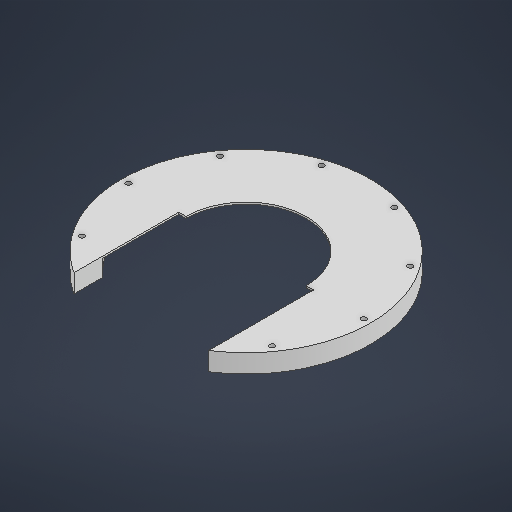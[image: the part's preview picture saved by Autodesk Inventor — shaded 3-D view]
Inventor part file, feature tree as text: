
AUTODESK INVENTOR PART (.ipt)
format: ipt  version: 2025 (Build 290162000, 162)  size: 236,544 bytes
history: native  units: in
note: dims shown in document units (in); Inventor stores cm internally (conversion verified against a paired STEP export)
features: sketch x5, extrude x3, hole x1
ambient origin geometry x8: Origin, YZ Plane, XZ Plane, XY Plane, X Axis, Y Axis, Z Axis, Center Point
bodies: Solid1 (feature_tree)
feature tree (9):
  extrude  "Extrusion1"  Depth=8.6614in
  hole  "Hole1"  [1 undecoded]
  extrude  "Extrusion3"  Depth=3.937in TaperAngle=360.0deg
  extrude  "Extrusion4"  Depth=0.315in
  sketch  "Sketch1"  dims[d0=10.6299in d1=8.6614in]
  sketch  "Sketch3"  dims[d8=0.1969in d9=3.937in d11=360.0deg]
  sketch  "Sketch Circular Pattern1"  dims[d2=0.7874in d3=0.0in d7=10.0394in]
  sketch  "Sketch4"  dims[d13=0.2165in d14=0.2362in d15=0.1575in d16=0.0787in d17=90.0deg d18=0.315in d19=0.8108in d21=5.1181in]
  sketch  "Sketch5"  dims[d22=0.0787in d23=0.0in d24=5.753in d25=13.7795in d26=0.0in d27=0.0in d28=0.0197in d29=0.0344in]
note: 1 required parameter value undecoded (feature->parameter linkage not recoverable at this tier; creation-order binding heuristic only, values carry confidence <= 0.55)
